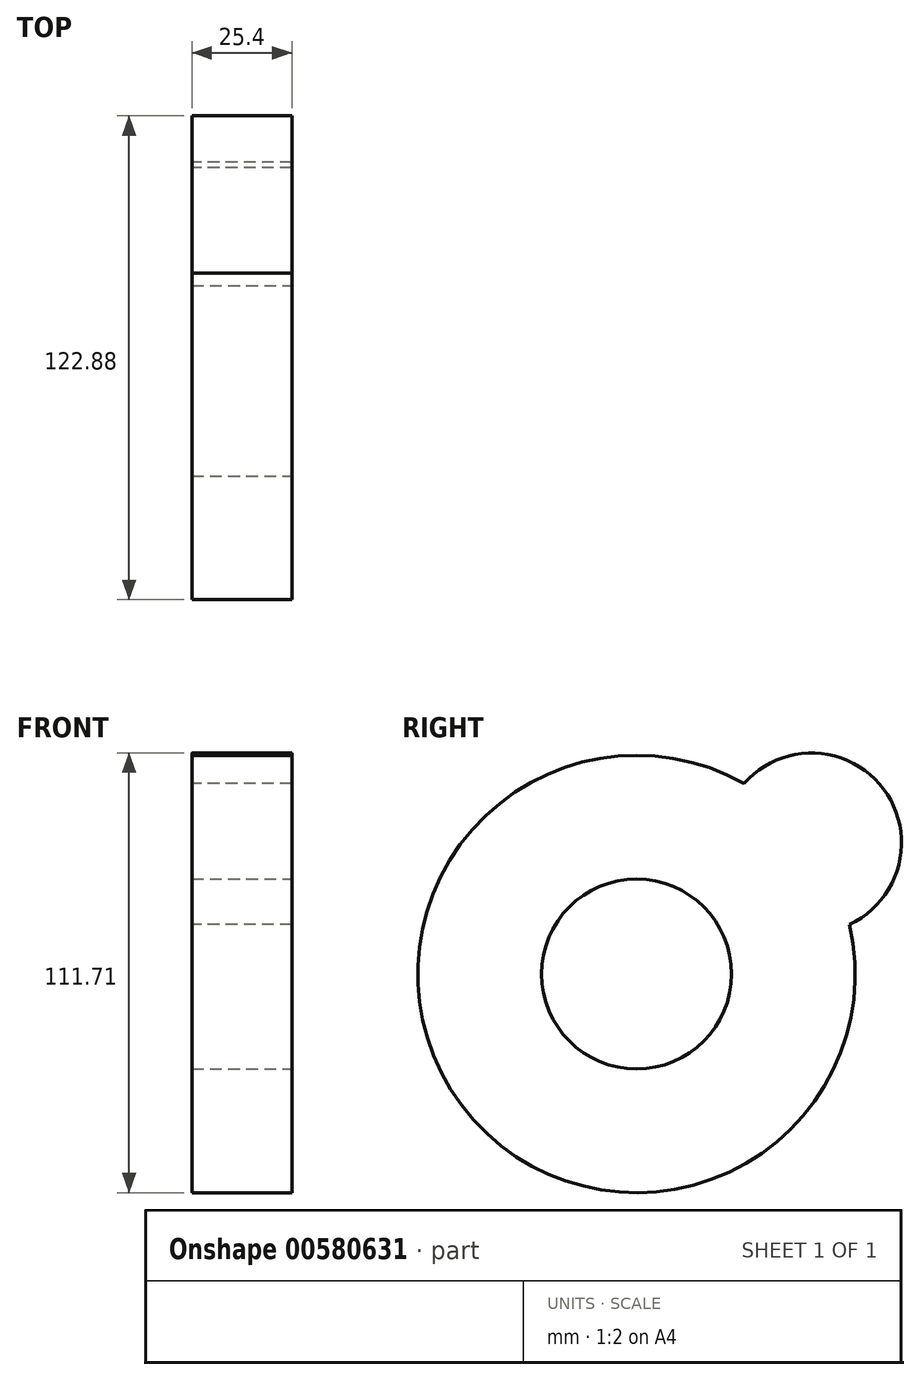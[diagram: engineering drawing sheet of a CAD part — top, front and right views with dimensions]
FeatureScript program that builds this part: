
annotation { "Feature Type Name" : "Feature", "Feature Type Description" : "" }
export const myFeature = defineFeature(function(context is Context, id is Id, definition is map)
    precondition{}
    {
        {
            var Q0;
            Q0=qCreatedBy(makeId("Right.planeOp"),FACE);
            var sketch = newSketch(context, id + "F0", { "sketchPlane" : qUnion([Q0])});
            skCircle(sketch, "E0", {"center": v(0, 0) * mm, "radius": 55.56 * mm});
            skCircle(sketch, "E1", {"center": v(44.47, 33.3) * mm, "radius": 22.85 * mm});
            skSolve(sketch);
        }
        {
            var Q0;
            Q0 = qSketchRegion(id + "F0", true);
            extrude(context, id + "F1", {"entities" : qUnion([Q0]), "depth" : 25.4 * mm, "offsetDistance" : 25.4 * mm});
        }
        {
            var Q0;
            Q0=makeQuery(id+"F1.opExtrude","CAP_FACE",FACE,{"disambiguationData":[OSD([sQuery(id+"F0.wireOp",EDGE,"E0"),sQuery(id+"F0.wireOp",EDGE,"E1")])],"isStart":false});
            var sketch = newSketch(context, id + "F2", { "sketchPlane" : qUnion([Q0])});
            skCircle(sketch, "E2", {"center": v(0, 0) * mm, "radius": 24.14 * mm});
            skSolve(sketch);
        }
        {
            var Q0;
            Q0 = qSketchRegion(id + "F2", true);
            var sketch = newSketch(context, id + "F3", { "sketchPlane" : qUnion([Q0])});
            skSolve(sketch);
        }
        {
            var Q0;
            Q0 = qSketchRegion(id + "F3", true);
            var Q1;
            Q1=makeQuery(id+"F3.imprint","IMPRINT",FACE,{"disambiguationData":[TD([[makeQuery(id+"F3.imprint","IMPRINT",EDGE,{"derivedFrom":makeQuery(id+"F2.imprint","IMPRINT",EDGE,{"derivedFrom":sQuery(id+"F2.wireOp",EDGE,"E2")})}),1.0]])]});
            extrude(context, id + "F4", {"entities" : qUnion([Q0, Q1]), "operationType" : NewBodyOperationType.REMOVE, "oppositeDirection" : true, "depth" : 25.4 * mm, "offsetDistance" : 25.4 * mm});
        }
        {
            var Q0;
            Q0 = qSketchRegion(id + "F2", true);
            var sketch = newSketch(context, id + "F5", { "sketchPlane" : qUnion([Q0])});
            skLineSegment(sketch, "E3.bottom", {"start": v(-33, 20.76) * mm, "end": v(26.4, 20.76) * mm});
            skLineSegment(sketch, "E3.top", {"start": v(-33, 111.2) * mm, "end": v(26.4, 111.2) * mm});
            skLineSegment(sketch, "E3.left", {"start": v(-33, 20.76) * mm, "end": v(-33, 111.2) * mm});
            skLineSegment(sketch, "E3.right", {"start": v(26.4, 20.76) * mm, "end": v(26.4, 111.2) * mm});
            skSolve(sketch);
        }
        {
            var Q0;
            Q0=sQuery(id+"F5.wireOp",EDGE,"E3.top");
            var Q1;
            Q1=sQuery(id+"F5.wireOp",EDGE,"E3.right");
            var Q2;
            Q2=sQuery(id+"F5.wireOp",EDGE,"E3.bottom");
            var Q3;
            Q3=sQuery(id+"F5.wireOp",EDGE,"E3.left");
            extrude(context, id + "F6", {"bodyType" : ToolBodyType.SURFACE, "surfaceEntities" : qUnion([Q0, Q1, Q2, Q3]), "depth" : 25 * mm, "offsetDistance" : 25 * mm});
        }
    });
